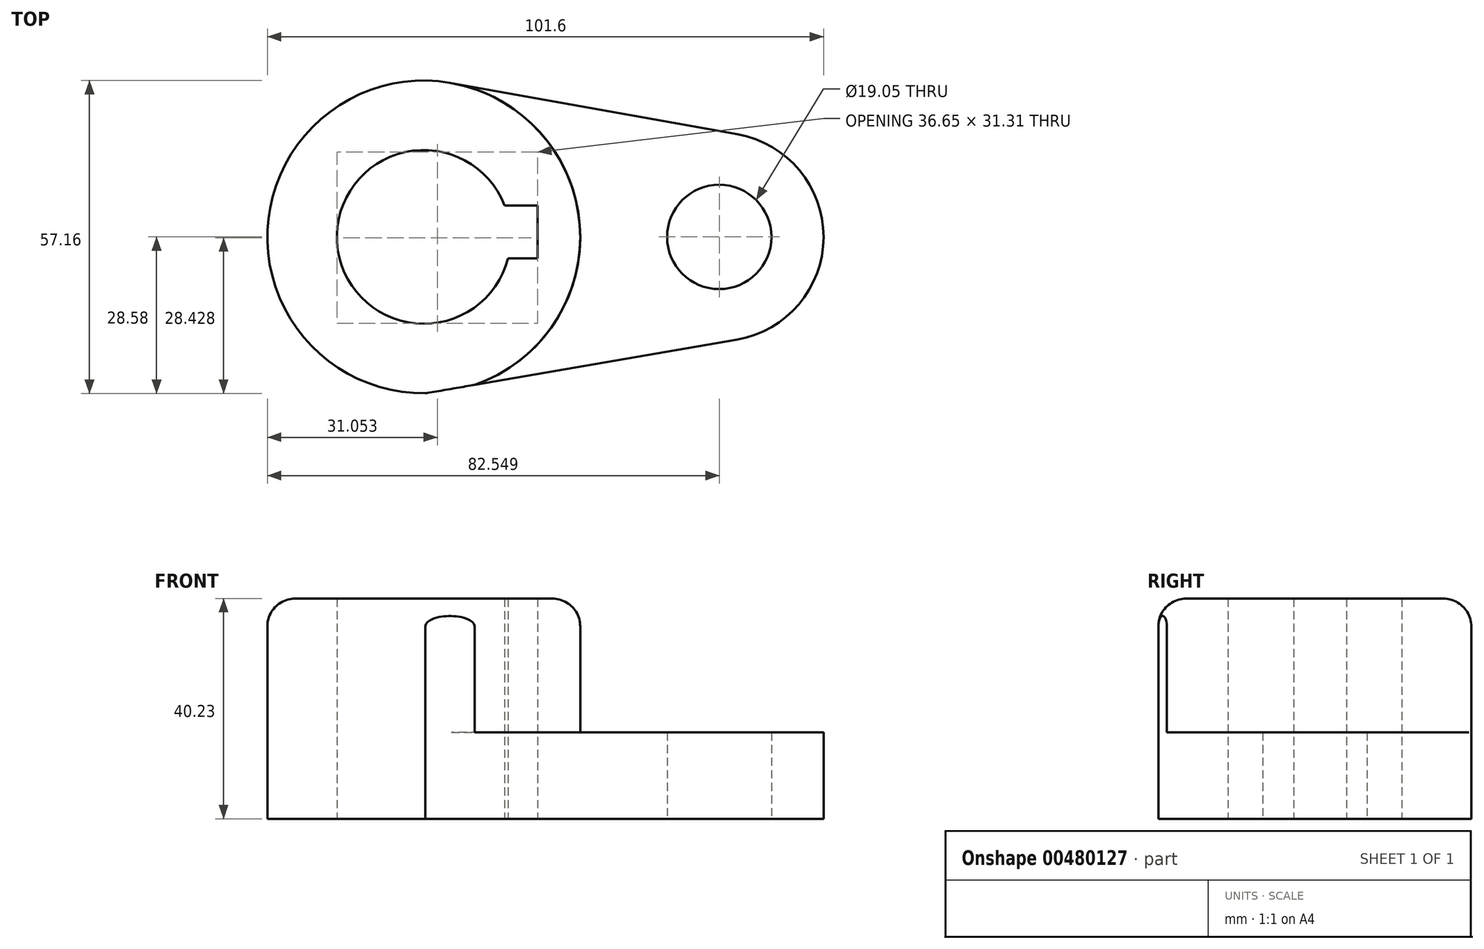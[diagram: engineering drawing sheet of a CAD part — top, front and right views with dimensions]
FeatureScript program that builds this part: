
annotation { "Feature Type Name" : "Feature", "Feature Type Description" : "" }
export const myFeature = defineFeature(function(context is Context, id is Id, definition is map)
    precondition{}
    {
        {
            var Q0;
            Q0=qCreatedBy(makeId("Top.planeOp"),FACE);
            var sketch = newSketch(context, id + "F0", { "sketchPlane" : qUnion([Q0])});
            skCircle(sketch, "E0", {"center": v(-51.88, 0) * mm, "radius": 28.58 * mm});
            skCircle(sketch, "E1", {"center": v(-51.88, 0) * mm, "radius": 15.88 * mm});
            skCircle(sketch, "E2", {"center": v(2.1, 0) * mm, "radius": 9.53 * mm});
            skCircle(sketch, "E3", {"center": v(2.1, 0) * mm, "radius": 19.05 * mm});
            skLineSegment(sketch, "E4", {"start": v(-46.83, 28.13) * mm, "end": v(5.46, 18.75) * mm});
            skLineSegment(sketch, "E5", {"start": v(-51.58, -28.57) * mm, "end": v(5.33, -18.77) * mm});
            skSolve(sketch);
        }
        {
            var Q0;
            Q0=makeQuery(id+"F0.imprint","IMPRINT",FACE,{"disambiguationData":[TD([[makeQuery(id+"F0.imprint","IMPRINT",EDGE,{"derivedFrom":sQuery(id+"F0.wireOp",EDGE,"E1")}),-1.0]])]});
            var sketch = newSketch(context, id + "F1", { "sketchPlane" : qUnion([Q0])});
            skLineSegment(sketch, "E6", {"start": v(-37.09, 5.77) * mm, "end": v(-31.07, 5.77) * mm});
            skLineSegment(sketch, "E7", {"start": v(-31.07, 5.77) * mm, "end": v(-31.07, -3.89) * mm});
            skLineSegment(sketch, "E8", {"start": v(-31.07, -3.89) * mm, "end": v(-36.48, -3.89) * mm});
            skSolve(sketch);
        }
        {
            var Q0;
            {var subQ5=sQuery(id+"F1.wireOp",EDGE,"E6");Q0=makeQuery(id+"F1.imprint","IMPRINT",FACE,{"disambiguationData":[TD([[makeQuery(id+"F1.imprint","IMPRINT",EDGE,{"derivedFrom":subQ5}),1.0]])]});}
            extrude(context, id + "F2", {"entities" : qUnion([Q0]), "depth" : 40.23 * mm});
        }
        {
            var Q0;
            Q0=makeQuery(id+"F0.imprint","IMPRINT",FACE,{"disambiguationData":[TD([[makeQuery(id+"F0.imprint","IMPRINT",EDGE,{"derivedFrom":sQuery(id+"F0.wireOp",EDGE,"E2")}),-1.0]])]});
            var Q1;
            {var subQ0=sQuery(id+"F0.wireOp",EDGE,"E4");Q1=makeQuery(id+"F0.imprint","IMPRINT",FACE,{"disambiguationData":[TD([[makeQuery(id+"F0.imprint","IMPRINT",EDGE,{"derivedFrom":subQ0}),-1.0]])]});}
            extrude(context, id + "F3", {"entities" : qUnion([Q0, Q1]), "operationType" : NewBodyOperationType.ADD, "depth" : 15.77 * mm});
        }
        {
            var Q0;
            Q0=makeQuery(id+"F2.opExtrude","CAP_EDGE",EDGE,{"disambiguationData":[OSD([sQuery(id+"F0.wireOp",EDGE,"E0")])],"isStart":false});
            fillet(context, id + "F4", {"entities" : qUnion([Q0]), "radius" : 5.08 * mm, "tangentPropagation" : true, "allowEdgeOverflow" : false});
        }
    });
